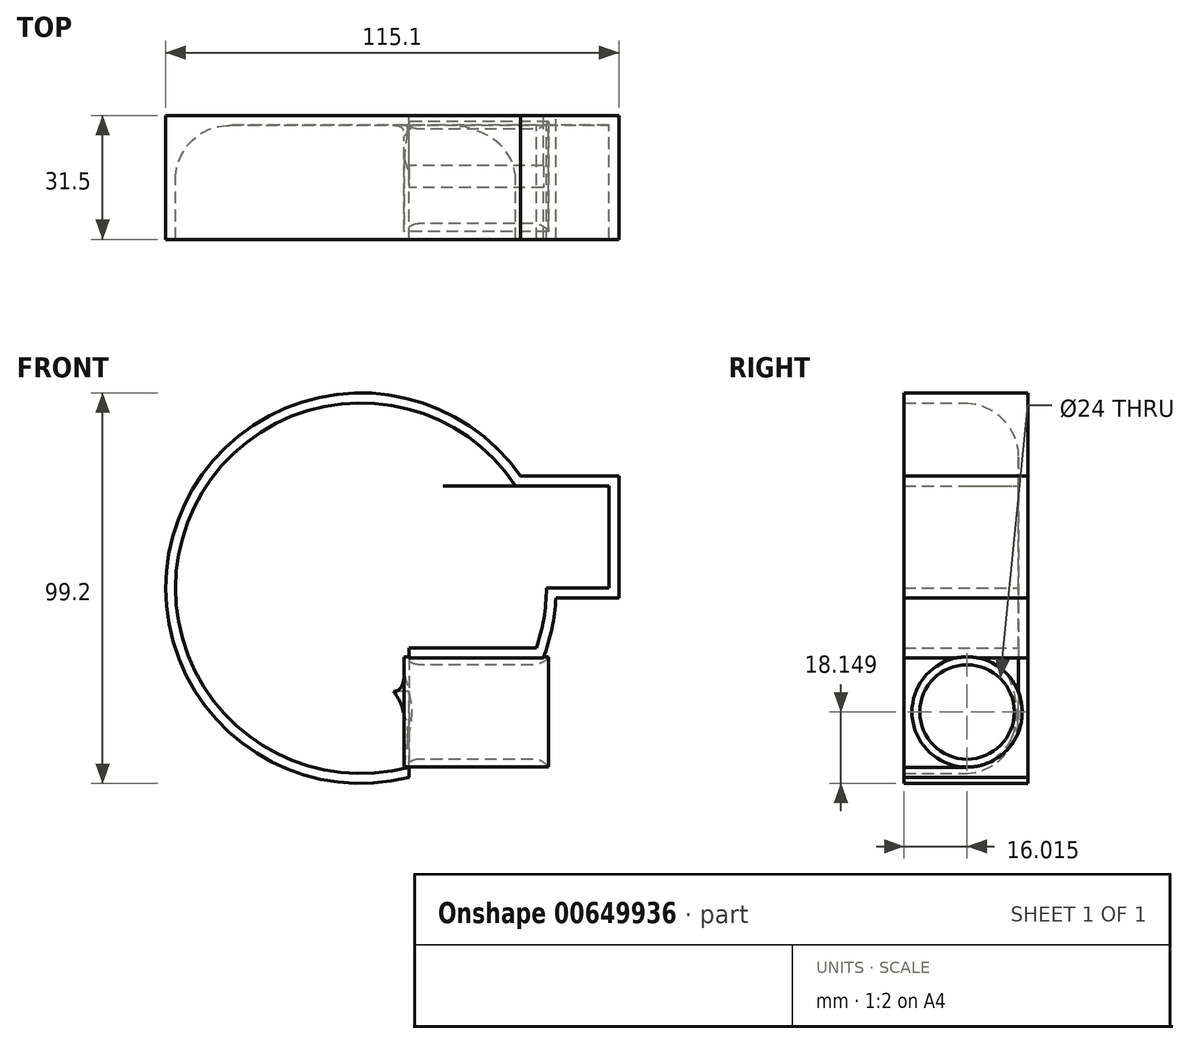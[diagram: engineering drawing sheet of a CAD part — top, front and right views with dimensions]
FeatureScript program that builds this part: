
annotation { "Feature Type Name" : "Feature", "Feature Type Description" : "" }
export const myFeature = defineFeature(function(context is Context, id is Id, definition is map)
    precondition{}
    {
        {
            var Q0;
            Q0=qCreatedBy(makeId("Front.planeOp"),FACE);
            var sketch = newSketch(context, id + "F0", { "sketchPlane" : qUnion([Q0])});
            skArc(sketch, "E0", {"start": v(40.21, -15.23) * mm, "mid": v(-29.26, 31.51) * mm, "end": v(12.21, -41.23) * mm});
            skLineSegment(sketch, "E1", {"start": v(43, 0) * mm, "end": v(63, 0) * mm});
            skLineSegment(sketch, "E2", {"start": v(63, 0) * mm, "end": v(63, 26) * mm});
            skLineSegment(sketch, "E3", {"start": v(63, 26) * mm, "end": v(34.25, 26) * mm});
            skLineSegment(sketch, "E4", {"start": v(43, 0) * mm, "end": v(43, 26) * mm});
            skArc(sketch, "E5.0", {"start": v(44.57, -15.23) * mm, "mid": v(-32.17, 34.4) * mm, "end": v(12.21, -45.49) * mm});
            skLineSegment(sketch, "E6", {"start": v(12.21, -41.23) * mm, "end": v(12.21, -15.23) * mm});
            skLineSegment(sketch, "E7", {"start": v(12.21, -15.23) * mm, "end": v(40.21, -15.23) * mm});
            skLineSegment(sketch, "E8", {"start": v(40.21, -15.23) * mm, "end": v(44.57, -15.23) * mm});
            skLineSegment(sketch, "E9", {"start": v(12.21, -41.23) * mm, "end": v(12.21, -45.49) * mm});
            skSolve(sketch);
        }
        {
            var Q0;
            Q0 = qSketchRegion(id + "F0", true);
            extrude(context, id + "F1", {"entities" : qUnion([Q0]), "depth" : 29 * mm, "offsetDistance" : 25 * mm});
        }
        {
            var Q0;
            Q0=qCreatedBy(makeId("Right.planeOp"),FACE);
            var sketch = newSketch(context, id + "F2", { "sketchPlane" : qUnion([Q0])});
            skCircle(sketch, "E10", {"center": v(-12.98, -31.45) * mm, "radius": 14 * mm});
            skCircle(sketch, "E11.0", {"center": v(-12.98, -31.45) * mm, "radius": 12 * mm});
            skSolve(sketch);
        }
        {
            var Q0;
            Q0=makeQuery(id+"F1.opExtrude","CAP_FACE",FACE,{"disambiguationData":[OSD([sQuery(id+"F0.wireOp",EDGE,"E1"),sQuery(id+"F0.wireOp",EDGE,"E2"),sQuery(id+"F0.wireOp",EDGE,"E3"),sQuery(id+"F0.wireOp",EDGE,"E5.0"),sQuery(id+"F0.wireOp",EDGE,"E6"),sQuery(id+"F0.wireOp",EDGE,"E7"),sQuery(id+"F0.wireOp",EDGE,"E8"),sQuery(id+"F0.wireOp",EDGE,"E9")])],"isStart":false});
            var Q1;
            Q1=makeQuery(id+"F1.opExtrude","SWEPT_FACE",FACE,{"disambiguationData":[OSD([sQuery(id+"F0.wireOp",EDGE,"E6"),sQuery(id+"F0.wireOp",EDGE,"E9")])]});
            shell(context, id + "F3", {"entities" : qUnion([Q0, Q1]), "thickness" : 2.5 * mm, "oppositeDirection" : true});
        }
        {
            var Q0;
            Q0=makeQuery(id+"F2.imprint","IMPRINT",FACE,{"disambiguationData":[TD([[makeQuery(id+"F2.imprint","IMPRINT",EDGE,{"derivedFrom":sQuery(id+"F2.wireOp",EDGE,"E10")}),1.0]])]});
            extrude(context, id + "F4", {"entities" : qUnion([Q0]), "operationType" : NewBodyOperationType.ADD, "depth" : 47.7 * mm, "offsetDistance" : 25 * mm, "hasSecondDirection" : true, "secondDirectionOppositeDirection" : false, "secondDirectionDepth" : 10 * mm});
        }
        {
            var Q0;
            Q0=makeQuery(id+"F4.opExtrude","CAP_EDGE",EDGE,{"disambiguationData":[OSD([sQuery(id+"F2.wireOp",EDGE,"E11.0")])],"isStart":true});
            fillet(context, id + "F5", {"entities" : qUnion([Q0]), "radius" : 5 * mm, "tangentPropagation" : true, "allowEdgeOverflow" : false});
        }
        {
            var Q0;
            Q0=makeQuery(id+"F5.opFillet","BLEND_EDGE",EDGE,{"blendedFrom":[makeQuery(id+"F4.opExtrude","CAP_EDGE",EDGE,{"disambiguationData":[OSD([sQuery(id+"F2.wireOp",EDGE,"E11.0")])],"isStart":true}),makeQuery(id+"F3.opShell","OFFSET_FACE",FACE,{"disambiguationData":[OSD([sQuery(id+"F0.wireOp",EDGE,"E1"),sQuery(id+"F0.wireOp",EDGE,"E2"),sQuery(id+"F0.wireOp",EDGE,"E3"),sQuery(id+"F0.wireOp",EDGE,"E5.0"),sQuery(id+"F0.wireOp",EDGE,"E6"),sQuery(id+"F0.wireOp",EDGE,"E7"),sQuery(id+"F0.wireOp",EDGE,"E8"),sQuery(id+"F0.wireOp",EDGE,"E9")])]})],"blendedInto":[makeQuery(id+"F3.opShell","OFFSET_FACE",FACE,{"disambiguationData":[OSD([sQuery(id+"F0.wireOp",EDGE,"E1"),sQuery(id+"F0.wireOp",EDGE,"E2"),sQuery(id+"F0.wireOp",EDGE,"E3"),sQuery(id+"F0.wireOp",EDGE,"E5.0"),sQuery(id+"F0.wireOp",EDGE,"E6"),sQuery(id+"F0.wireOp",EDGE,"E7"),sQuery(id+"F0.wireOp",EDGE,"E8"),sQuery(id+"F0.wireOp",EDGE,"E9")])]})]});
            fillet(context, id + "F6", {"entities" : qUnion([Q0]), "radius" : 5 * mm, "tangentPropagation" : true, "allowEdgeOverflow" : false});
        }
        {
            var Q0;
            Q0=makeQuery(id+"F4.opExtrude","CAP_EDGE",EDGE,{"disambiguationData":[OSD([sQuery(id+"F2.wireOp",EDGE,"E11.0")])],"isStart":false});
            fillet(context, id + "F7", {"entities" : qUnion([Q0]), "radius" : 5 * mm, "tangentPropagation" : true, "allowEdgeOverflow" : false});
        }
        {
            var Q0;
            {var subQ0=sQuery(id+"F0.wireOp",EDGE,"E5.0");Q0=makeQuery(id+"F3.opShell","OFFSET_EDGE",EDGE,{"disambiguationData":[OSD([subQ0]),TDD([makeQuery(id+"F1.opExtrude","CAP_EDGE",EDGE,{"disambiguationData":[OSD([subQ0]),TDD([makeQuery(id+"F0.imprint","IMPRINT",EDGE,{"disambiguationData":[TD([[makeQuery(id+"F0.imprint","INTERSECT",VERTEX,{"derivedFrom":[subQ0,sQuery(id+"F0.wireOp",EDGE,"E9")]}),1.0]])],"derivedFrom":subQ0})])],"isStart":true})])]});}
            fillet(context, id + "F8", {"entities" : qUnion([Q0]), "radius" : 13.76 * mm, "tangentPropagation" : true, "allowEdgeOverflow" : false});
        }
    });
